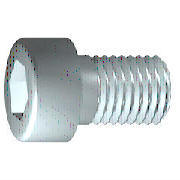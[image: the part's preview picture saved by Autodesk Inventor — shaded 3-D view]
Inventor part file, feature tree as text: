
AUTODESK INVENTOR PART (.ipt)
format: ipt  version: 2022 (Build 260153000, 153)  size: 188,928 bytes
history: native  units: mm (DEFAULTED — no unit token found)
features: sketch x2, extrude x1, plane x1, fillet x1
ambient origin geometry x7: Origin, YZ Plane, XY Plane, X Axis, Y Axis, Z Axis, Center Point
bodies: Solid1 (feature_tree), Body (feature_tree)
feature tree (5):
  extrude  "Slot"  Depth=4.0mm
  plane  "Work Plane1"
  fillet  "Fillet2"  Radius=4.0mm
  sketch  "Sketch1"  dims[d1=23.25mm d2=0.429515mm d3=4.0mm]
  sketch  "Sketch2"  dims[d4=2.0mm d5=60.0deg d6=4.0mm d7=4.0mm d8=3.464102mm d9=7.0mm d10=90.0deg d11=10.0mm d12=0.0mm d13=23.25mm d14=0.0mm d15=0.429415mm d16=0.429415mm d17=0.4mm d19=0.0mm d26=25.0mm d27=45.0deg d28=0.0mm d29=0.0mm d30=0.1mm]
